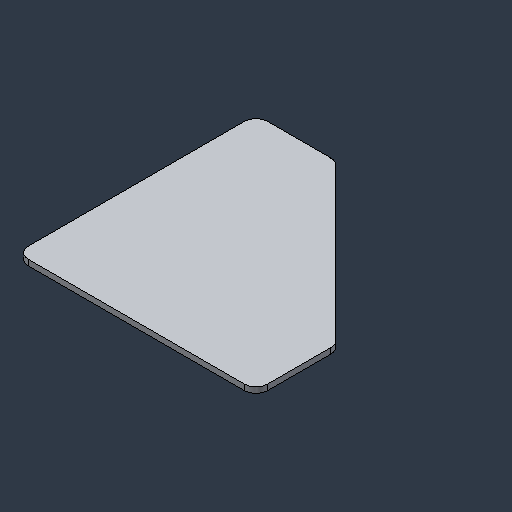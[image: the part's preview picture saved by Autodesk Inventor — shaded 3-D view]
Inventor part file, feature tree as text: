
AUTODESK INVENTOR PART (.ipt)
format: ipt  version: 2024.3 (Build 283343000, 343)  size: 80,384 bytes
history: native  units: mm (DEFAULTED — no unit token found)
features: fillet x1
ambient origin geometry x8: Origin, YZ Plane, XZ Plane, XY Plane, X Axis, Y Axis, Z Axis, Center Point
bodies: Solid1 (feature_tree)
feature tree (1):
  fillet  "Fillet1"  [1 undecoded]
note: 1 required parameter value undecoded (feature->parameter linkage not recoverable at this tier; creation-order binding heuristic only, values carry confidence <= 0.55)
